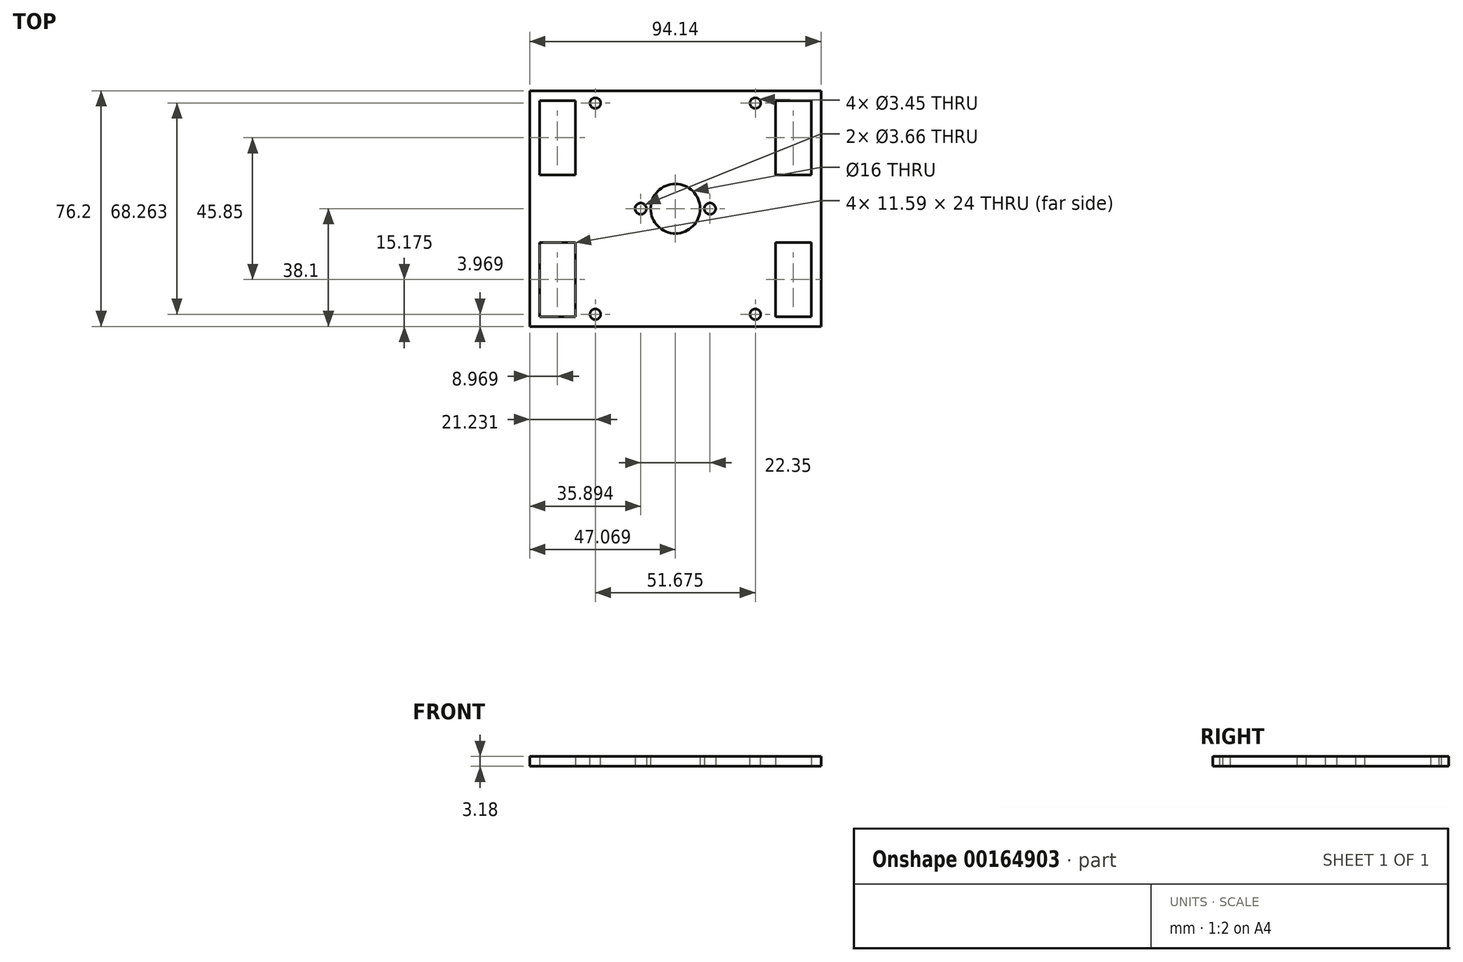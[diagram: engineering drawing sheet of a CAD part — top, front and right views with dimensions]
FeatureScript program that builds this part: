
annotation { "Feature Type Name" : "Feature", "Feature Type Description" : "" }
export const myFeature = defineFeature(function(context is Context, id is Id, definition is map)
    precondition{}
    {
        {
            var Q0;
            Q0=qCreatedBy(makeId("Top.planeOp"),FACE);
            var sketch = newSketch(context, id + "F0", { "sketchPlane" : qUnion([Q0])});
            skLineSegment(sketch, "E0.bottom", {"start": v(0, 0) * mm, "end": v(94.14, 0) * mm});
            skLineSegment(sketch, "E0.top", {"start": v(0, -76.2) * mm, "end": v(94.14, -76.2) * mm});
            skLineSegment(sketch, "E0.left", {"start": v(0, 0) * mm, "end": v(0, -76.2) * mm});
            skLineSegment(sketch, "E0.right", {"start": v(94.14, 0) * mm, "end": v(94.14, -76.2) * mm});
            skLineSegment(sketch, "E1", {"start": v(47.07, 0) * mm, "end": v(47.07, -76.2) * mm, "construction": true});
            skLineSegment(sketch, "E2.bottom", {"start": v(85.17, -15.18) * mm, "end": v(8.97, -15.18) * mm, "construction": true});
            skLineSegment(sketch, "E2.top", {"start": v(85.17, -61.03) * mm, "end": v(8.97, -61.03) * mm, "construction": true});
            skLineSegment(sketch, "E2.left", {"start": v(85.17, -15.18) * mm, "end": v(85.17, -61.03) * mm, "construction": true});
            skLineSegment(sketch, "E2.right", {"start": v(8.97, -15.18) * mm, "end": v(8.97, -61.03) * mm, "construction": true});
            skPoint(sketch, "E2.middle", {"position": v(47.07, -38.1) * mm});
            skLineSegment(sketch, "E3.bottom", {"start": v(90.96, -3.18) * mm, "end": v(79.38, -3.18) * mm});
            skLineSegment(sketch, "E3.top", {"start": v(90.96, -27.18) * mm, "end": v(79.38, -27.18) * mm});
            skLineSegment(sketch, "E3.left", {"start": v(90.96, -3.18) * mm, "end": v(90.96, -27.17) * mm});
            skLineSegment(sketch, "E3.right", {"start": v(79.38, -3.18) * mm, "end": v(79.38, -27.18) * mm});
            skPoint(sketch, "E3.middle", {"position": v(85.17, -15.18) * mm});
            skLineSegment(sketch, "E4.bottom", {"start": v(90.96, -73.03) * mm, "end": v(79.37, -73.03) * mm});
            skLineSegment(sketch, "E4.top", {"start": v(90.96, -49.03) * mm, "end": v(79.37, -49.03) * mm});
            skLineSegment(sketch, "E4.left", {"start": v(90.96, -73.03) * mm, "end": v(90.96, -49.03) * mm});
            skLineSegment(sketch, "E4.right", {"start": v(79.37, -73.03) * mm, "end": v(79.37, -49.03) * mm});
            skPoint(sketch, "E4.middle", {"position": v(85.17, -61.03) * mm});
            skLineSegment(sketch, "E5.bottom", {"start": v(3.17, -73.03) * mm, "end": v(14.76, -73.03) * mm});
            skLineSegment(sketch, "E5.top", {"start": v(3.17, -49.03) * mm, "end": v(14.76, -49.03) * mm});
            skLineSegment(sketch, "E5.left", {"start": v(3.17, -73.03) * mm, "end": v(3.17, -49.03) * mm});
            skLineSegment(sketch, "E5.right", {"start": v(14.76, -73.03) * mm, "end": v(14.76, -49.03) * mm});
            skPoint(sketch, "E5.middle", {"position": v(8.97, -61.03) * mm});
            skLineSegment(sketch, "E6.bottom", {"start": v(3.17, -27.17) * mm, "end": v(14.76, -27.17) * mm});
            skLineSegment(sketch, "E6.top", {"start": v(3.17, -3.18) * mm, "end": v(14.76, -3.18) * mm});
            skLineSegment(sketch, "E6.left", {"start": v(3.17, -27.17) * mm, "end": v(3.17, -3.18) * mm});
            skLineSegment(sketch, "E6.right", {"start": v(14.76, -27.17) * mm, "end": v(14.76, -3.18) * mm});
            skPoint(sketch, "E6.middle", {"position": v(8.97, -15.18) * mm});
            skCircle(sketch, "E7", {"center": v(47.07, -38.1) * mm, "radius": 8 * mm});
            skLineSegment(sketch, "E8", {"start": v(35.9, -38.1) * mm, "end": v(58.24, -38.1) * mm, "construction": true});
            skCircle(sketch, "E9", {"center": v(35.9, -38.1) * mm, "radius": 1.83 * mm});
            skCircle(sketch, "E10", {"center": v(58.24, -38.1) * mm, "radius": 1.83 * mm});
            skSolve(sketch);
        }
        {
            var Q0;
            Q0=qSketchRegion(id+"F0",true);
            extrude(context, id + "F1", {"entities" : qUnion([Q0]), "depth" : 3.17 * mm});
        }
        {
            var Q0;
            Q0=makeQuery(id+"F1.opExtrude","CAP_FACE",FACE,{"disambiguationData":[OSD([sQuery(id+"F0.wireOp",EDGE,"E0.bottom"),sQuery(id+"F0.wireOp",EDGE,"E0.top"),sQuery(id+"F0.wireOp",EDGE,"E0.left"),sQuery(id+"F0.wireOp",EDGE,"E0.right"),sQuery(id+"F0.wireOp",EDGE,"E3.bottom"),sQuery(id+"F0.wireOp",EDGE,"E3.top"),sQuery(id+"F0.wireOp",EDGE,"E3.left"),sQuery(id+"F0.wireOp",EDGE,"E3.right"),sQuery(id+"F0.wireOp",EDGE,"E4.bottom"),sQuery(id+"F0.wireOp",EDGE,"E4.top"),sQuery(id+"F0.wireOp",EDGE,"E4.left"),sQuery(id+"F0.wireOp",EDGE,"E4.right"),sQuery(id+"F0.wireOp",EDGE,"E5.bottom"),sQuery(id+"F0.wireOp",EDGE,"E5.top"),sQuery(id+"F0.wireOp",EDGE,"E5.left"),sQuery(id+"F0.wireOp",EDGE,"E5.right"),sQuery(id+"F0.wireOp",EDGE,"E6.bottom"),sQuery(id+"F0.wireOp",EDGE,"E6.top"),sQuery(id+"F0.wireOp",EDGE,"E6.left"),sQuery(id+"F0.wireOp",EDGE,"E6.right"),sQuery(id+"F0.wireOp",EDGE,"E7"),sQuery(id+"F0.wireOp",EDGE,"E9"),sQuery(id+"F0.wireOp",EDGE,"E10")])],"isStart":false});
            var sketch = newSketch(context, id + "F2", { "sketchPlane" : qUnion([Q0])});
            skLineSegment(sketch, "E11", {"start": v(8.97, -73.03) * mm, "end": v(8.97, -72.23) * mm, "construction": true});
            skLineSegment(sketch, "E12", {"start": v(8.97, -72.23) * mm, "end": v(21.23, -72.23) * mm, "construction": true});
            skLineSegment(sketch, "E13.bottom", {"start": v(21.23, -72.23) * mm, "end": v(72.9, -72.23) * mm, "construction": true});
            skLineSegment(sketch, "E13.top", {"start": v(21.23, -3.97) * mm, "end": v(72.9, -3.97) * mm, "construction": true});
            skLineSegment(sketch, "E13.left", {"start": v(21.23, -72.23) * mm, "end": v(21.23, -3.97) * mm, "construction": true});
            skLineSegment(sketch, "E13.right", {"start": v(72.9, -72.23) * mm, "end": v(72.9, -3.97) * mm, "construction": true});
            skPoint(sketch, "E13.middle", {"position": v(47.07, -38.1) * mm});
            skCircle(sketch, "E14", {"center": v(21.23, -3.97) * mm, "radius": 1.73 * mm});
            skCircle(sketch, "E15", {"center": v(72.9, -3.97) * mm, "radius": 1.73 * mm});
            skCircle(sketch, "E16", {"center": v(72.9, -72.23) * mm, "radius": 1.73 * mm});
            skCircle(sketch, "E17", {"center": v(21.23, -72.23) * mm, "radius": 1.73 * mm});
            skSolve(sketch);
        }
        {
            var Q0;
            Q0 = qSketchRegion(id + "F2", true);
            var Q1;
            Q1=makeQuery(id+"F1.opExtrude","CAP_FACE",FACE,{"disambiguationData":[OSD([sQuery(id+"F0.wireOp",EDGE,"E0.bottom"),sQuery(id+"F0.wireOp",EDGE,"E0.top"),sQuery(id+"F0.wireOp",EDGE,"E0.left"),sQuery(id+"F0.wireOp",EDGE,"E0.right"),sQuery(id+"F0.wireOp",EDGE,"E3.bottom"),sQuery(id+"F0.wireOp",EDGE,"E3.top"),sQuery(id+"F0.wireOp",EDGE,"E3.left"),sQuery(id+"F0.wireOp",EDGE,"E3.right"),sQuery(id+"F0.wireOp",EDGE,"E4.bottom"),sQuery(id+"F0.wireOp",EDGE,"E4.top"),sQuery(id+"F0.wireOp",EDGE,"E4.left"),sQuery(id+"F0.wireOp",EDGE,"E4.right"),sQuery(id+"F0.wireOp",EDGE,"E5.bottom"),sQuery(id+"F0.wireOp",EDGE,"E5.top"),sQuery(id+"F0.wireOp",EDGE,"E5.left"),sQuery(id+"F0.wireOp",EDGE,"E5.right"),sQuery(id+"F0.wireOp",EDGE,"E6.bottom"),sQuery(id+"F0.wireOp",EDGE,"E6.top"),sQuery(id+"F0.wireOp",EDGE,"E6.left"),sQuery(id+"F0.wireOp",EDGE,"E6.right"),sQuery(id+"F0.wireOp",EDGE,"E7"),sQuery(id+"F0.wireOp",EDGE,"E9"),sQuery(id+"F0.wireOp",EDGE,"E10")])],"isStart":true});
            extrude(context, id + "F3", {"entities" : qUnion([Q0]), "operationType" : NewBodyOperationType.REMOVE, "endBound" : BoundingType.UP_TO_SURFACE, "oppositeDirection" : true, "endBoundEntityFace" : qUnion([Q1]), "depth" : 25.4 * mm});
        }
    });
